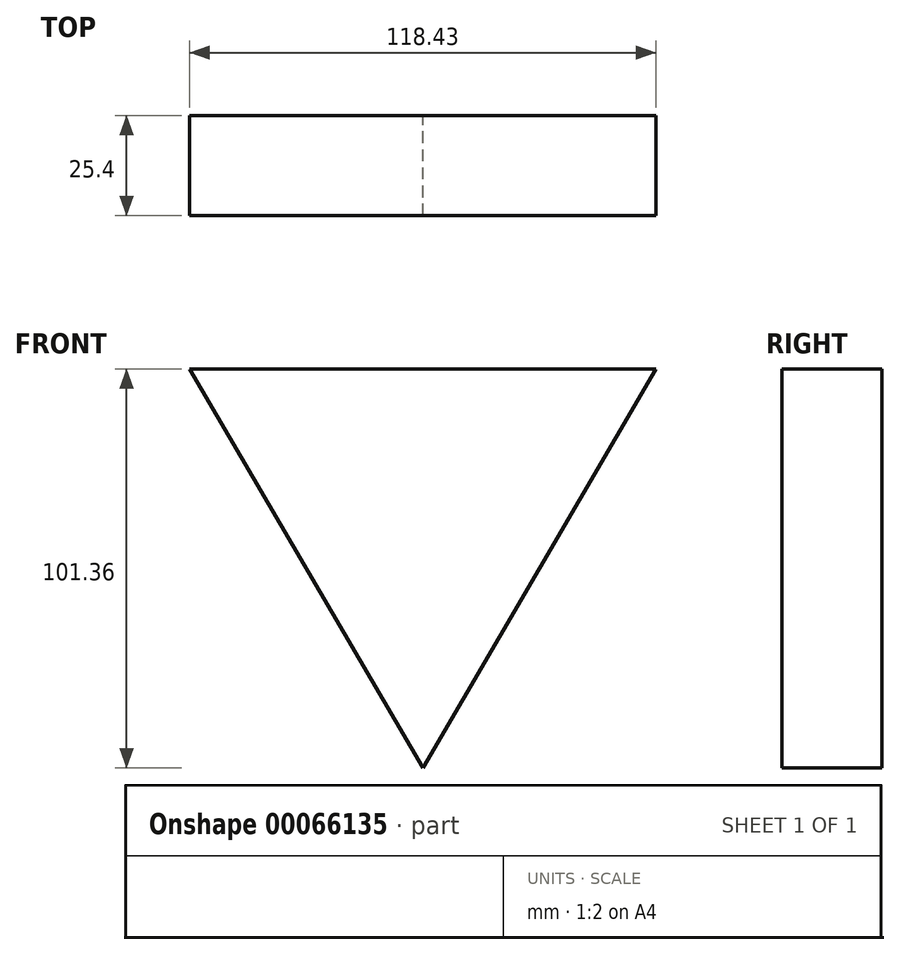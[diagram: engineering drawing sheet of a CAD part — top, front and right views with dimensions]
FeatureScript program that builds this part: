
annotation { "Feature Type Name" : "Feature", "Feature Type Description" : "" }
export const myFeature = defineFeature(function(context is Context, id is Id, definition is map)
    precondition{}
    {
        {
            var Q0;
            Q0=qCreatedBy(makeId("Front.planeOp"),FACE);
            var sketch = newSketch(context, id + "F0", { "sketchPlane" : qUnion([Q0])});
            skLineSegment(sketch, "E0", {"start": v(-59.3, 43.4) * mm, "end": v(59.14, 43.4) * mm});
            skLineSegment(sketch, "E1", {"start": v(59.14, 43.4) * mm, "end": v(0, -57.96) * mm});
            skLineSegment(sketch, "E2", {"start": v(0, -57.96) * mm, "end": v(-59.3, 43.4) * mm});
            skLineSegment(sketch, "E3", {"start": v(0, 43.4) * mm, "end": v(0, -57.96) * mm});
            skLineSegment(sketch, "E4", {"start": v(-33.9, 0) * mm, "end": v(38.34, 0) * mm});
            skLineSegment(sketch, "E5", {"start": v(38.34, 0) * mm, "end": v(15.4, 0) * mm});
            skSolve(sketch);
        }
        {
            var Q0;
            Q0 = qSketchRegion(id + "F0", true);
            extrude(context, id + "F1", {"entities" : qUnion([Q0]), "depth" : 25.4 * mm});
        }
    });
